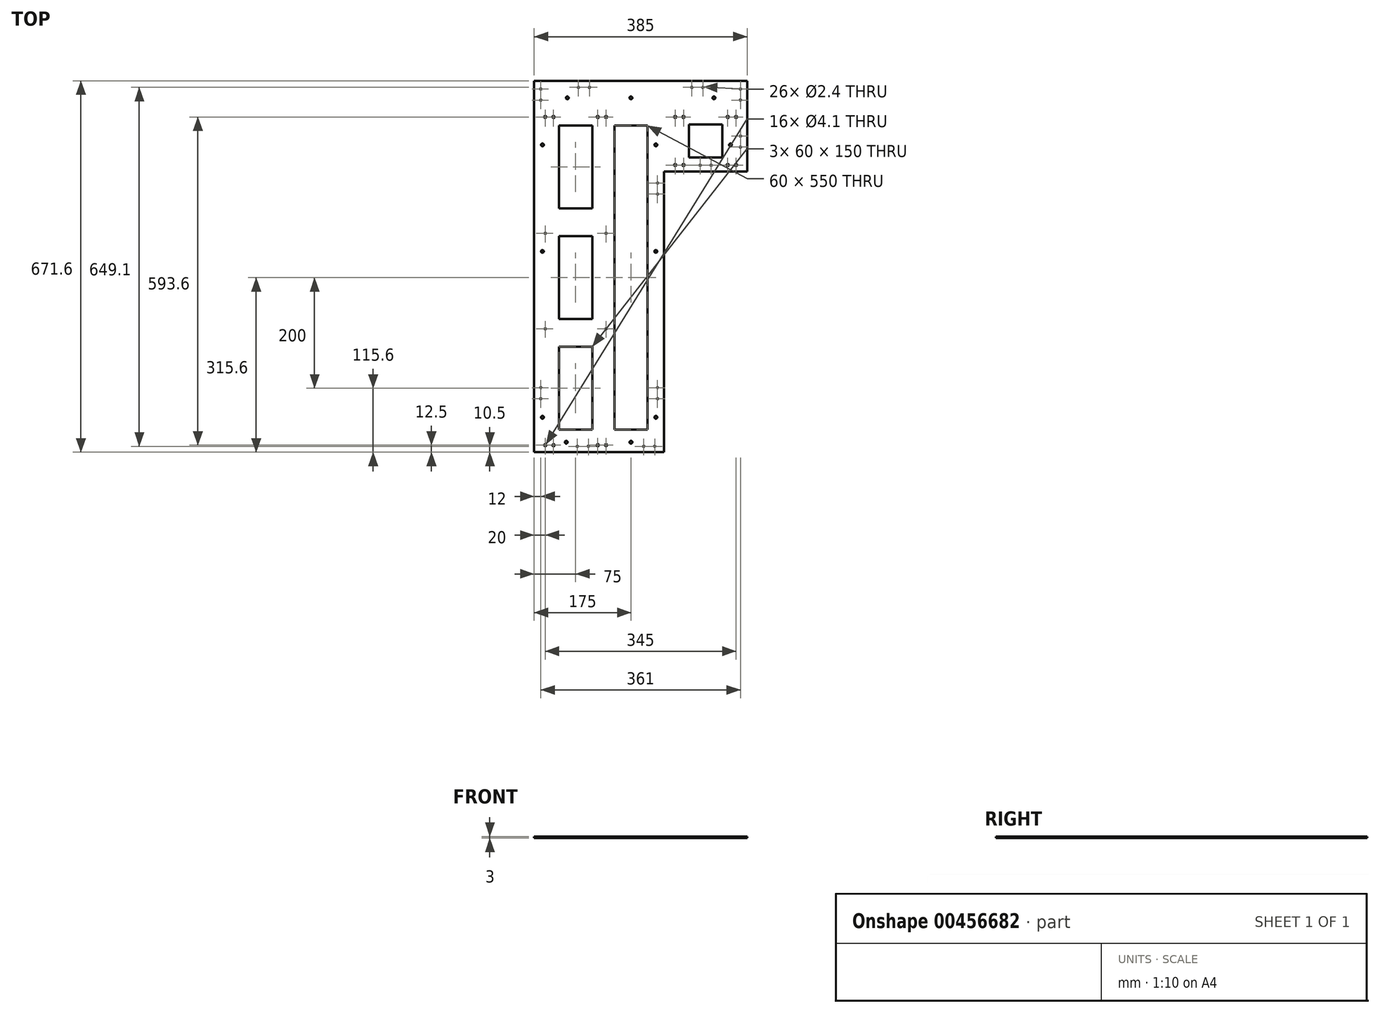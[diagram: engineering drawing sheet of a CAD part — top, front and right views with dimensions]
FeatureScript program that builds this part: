
annotation { "Feature Type Name" : "Feature", "Feature Type Description" : "" }
export const myFeature = defineFeature(function(context is Context, id is Id, definition is map)
    precondition{}
    {
        {
            var Q0;
            Q0=qCreatedBy(makeId("Top.planeOp"),FACE);
            var sketch = newSketch(context, id + "F0", { "sketchPlane" : qUnion([Q0])});
            skLineSegment(sketch, "E0.bottom", {"start": v(192.5, -53) * mm, "end": v(-192.5, -53) * mm});
            skLineSegment(sketch, "E0.top", {"start": v(192.5, 53) * mm, "end": v(-192.5, 53) * mm});
            skLineSegment(sketch, "E0.left", {"start": v(192.5, -53) * mm, "end": v(192.5, 53) * mm});
            skLineSegment(sketch, "E0.right", {"start": v(-192.5, -53) * mm, "end": v(-192.5, 53) * mm});
            skPoint(sketch, "E0.middle", {"position": v(0, 0) * mm});
            skCircle(sketch, "E1", {"center": v(-172.5, 43.5) * mm, "radius": 2.05 * mm});
            skCircle(sketch, "E2", {"center": v(-157.5, 43.5) * mm, "radius": 2.05 * mm});
            skLineSegment(sketch, "E3", {"start": v(-42.5, 73.43) * mm, "end": v(-42.5, -580.65) * mm, "construction": true});
            skLineSegment(sketch, "E4", {"start": v(42.5, 94.16) * mm, "end": v(42.5, -111.22) * mm, "construction": true});
            skCircle(sketch, "E5", {"center": v(-77.5, 43.5) * mm, "radius": 2.05 * mm});
            skCircle(sketch, "E6", {"center": v(-62.5, 43.5) * mm, "radius": 2.05 * mm});
            skCircle(sketch, "E7", {"center": v(62.5, 43.5) * mm, "radius": 2.05 * mm});
            skCircle(sketch, "E8", {"center": v(77.5, 43.5) * mm, "radius": 2.05 * mm});
            skCircle(sketch, "E9", {"center": v(157.5, 43.5) * mm, "radius": 2.05 * mm});
            skCircle(sketch, "E10", {"center": v(172.5, 43.5) * mm, "radius": 2.05 * mm});
            skLineSegment(sketch, "E11", {"start": v(202.9, -33.92) * mm, "end": v(25.15, -33.92) * mm, "construction": true});
            skCircle(sketch, "E12", {"center": v(172.5, -43.42) * mm, "radius": 2.05 * mm});
            skCircle(sketch, "E13", {"center": v(157.5, -43.42) * mm, "radius": 2.05 * mm});
            skCircle(sketch, "E14", {"center": v(62.5, -43.42) * mm, "radius": 2.05 * mm});
            skCircle(sketch, "E15", {"center": v(77.5, -43.42) * mm, "radius": 2.05 * mm});
            skLineSegment(sketch, "E16.bottom", {"start": v(-192.5, -53) * mm, "end": v(42.5, -53) * mm});
            skLineSegment(sketch, "E16.top", {"start": v(-192.5, -559.6) * mm, "end": v(42.5, -559.6) * mm});
            skLineSegment(sketch, "E16.left", {"start": v(-192.5, -53) * mm, "end": v(-192.5, -559.6) * mm});
            skLineSegment(sketch, "E16.right", {"start": v(42.5, -53) * mm, "end": v(42.5, -559.6) * mm});
            skLineSegment(sketch, "E17", {"start": v(-218.51, -539.6) * mm, "end": v(119.99, -539.6) * mm, "construction": true});
            skCircle(sketch, "E18", {"center": v(-172.5, -550.1) * mm, "radius": 2.05 * mm});
            skCircle(sketch, "E19", {"center": v(-157.5, -550.1) * mm, "radius": 2.05 * mm});
            skCircle(sketch, "E20", {"center": v(-77.5, -550.1) * mm, "radius": 2.05 * mm});
            skCircle(sketch, "E21", {"center": v(-62.5, -550.1) * mm, "radius": 2.05 * mm});
            skLineSegment(sketch, "E22", {"start": v(-117.5, 57.85) * mm, "end": v(-117.5, 33.54) * mm, "construction": true});
            skLineSegment(sketch, "E23", {"start": v(-153.12, 33) * mm, "end": v(-174.42, 33) * mm, "construction": true});
            skCircle(sketch, "E24", {"center": v(-172.5, -167) * mm, "radius": 1.2 * mm});
            skLineSegment(sketch, "E25", {"start": v(-176.5, -137.08) * mm, "end": v(-176.5, -144.67) * mm, "construction": true});
            skCircle(sketch, "E26", {"center": v(-172.5, -339.6) * mm, "radius": 1.2 * mm});
            skCircle(sketch, "E27", {"center": v(-62.5, -167) * mm, "radius": 1.2 * mm});
            skCircle(sketch, "E28", {"center": v(-62.5, -339.6) * mm, "radius": 1.2 * mm});
            skCircle(sketch, "E29", {"center": v(-177.5, -199.6) * mm, "radius": 2.5 * mm});
            skCircle(sketch, "E30", {"center": v(-134.5, -544.6) * mm, "radius": 2.5 * mm});
            skLineSegment(sketch, "E31.top", {"start": v(-192.5, -562.6) * mm, "end": v(42.5, -562.6) * mm});
            skLineSegment(sketch, "E31.left", {"start": v(-192.5, -559.6) * mm, "end": v(-192.5, -562.6) * mm});
            skLineSegment(sketch, "E31.right", {"start": v(42.5, -559.6) * mm, "end": v(42.5, -562.6) * mm});
            skCircle(sketch, "E32", {"center": v(-177.5, -499.6) * mm, "radius": 2.5 * mm});
            skCircle(sketch, "E33", {"center": v(-177.5, -7) * mm, "radius": 2.5 * mm});
            skCircle(sketch, "E34", {"center": v(27.5, -199.6) * mm, "radius": 2.5 * mm});
            skCircle(sketch, "E35", {"center": v(-17.5, -544.6) * mm, "radius": 2.5 * mm});
            skCircle(sketch, "E36", {"center": v(27.5, -499.6) * mm, "radius": 2.5 * mm});
            skCircle(sketch, "E37", {"center": v(27.5, -7) * mm, "radius": 2.5 * mm});
            skCircle(sketch, "E38", {"center": v(-132.5, 78) * mm, "radius": 2.5 * mm});
            skCircle(sketch, "E39", {"center": v(132.5, 78) * mm, "radius": 2.5 * mm});
            skCircle(sketch, "E40", {"center": v(-17.5, 78) * mm, "radius": 2.5 * mm});
            skLineSegment(sketch, "E41.bottom", {"start": v(42.5, -53) * mm, "end": v(192.5, -53) * mm});
            skLineSegment(sketch, "E41.top", {"start": v(42.5, -55) * mm, "end": v(192.5, -55) * mm});
            skLineSegment(sketch, "E41.left", {"start": v(42.5, -53) * mm, "end": v(42.5, -55) * mm});
            skLineSegment(sketch, "E41.right", {"start": v(192.5, -53) * mm, "end": v(192.5, -55) * mm});
            skLineSegment(sketch, "E42", {"start": v(-192.5, 53) * mm, "end": v(-192.5, 109) * mm});
            skLineSegment(sketch, "E43", {"start": v(-192.5, 109) * mm, "end": v(192.5, 109) * mm});
            skLineSegment(sketch, "E44", {"start": v(192.5, 109) * mm, "end": v(192.5, 53) * mm});
            skCircle(sketch, "E45", {"center": v(162.5, -7) * mm, "radius": 2.5 * mm});
            skSolve(sketch);
        }
        {
            var Q0;
            Q0=qSketchRegion(id+"F0",true);
            extrude(context, id + "F1", {"entities" : qUnion([Q0]), "depth" : 3 * mm});
        }
        {
            var Q0;
            Q0=makeQuery(id+"F1.opExtrude","CAP_FACE",FACE,{"disambiguationData":[OSD([sQuery(id+"F0.wireOp",EDGE,"E0.bottom"),sQuery(id+"F0.wireOp",EDGE,"E0.top"),sQuery(id+"F0.wireOp",EDGE,"E0.left"),sQuery(id+"F0.wireOp",EDGE,"E0.right"),sQuery(id+"F0.wireOp",EDGE,"E1"),sQuery(id+"F0.wireOp",EDGE,"E2"),sQuery(id+"F0.wireOp",EDGE,"E5"),sQuery(id+"F0.wireOp",EDGE,"E6"),sQuery(id+"F0.wireOp",EDGE,"E7"),sQuery(id+"F0.wireOp",EDGE,"E8"),sQuery(id+"F0.wireOp",EDGE,"E9"),sQuery(id+"F0.wireOp",EDGE,"E10"),sQuery(id+"F0.wireOp",EDGE,"E12"),sQuery(id+"F0.wireOp",EDGE,"E13"),sQuery(id+"F0.wireOp",EDGE,"E14"),sQuery(id+"F0.wireOp",EDGE,"E15"),sQuery(id+"F0.wireOp",EDGE,"E16.top"),sQuery(id+"F0.wireOp",EDGE,"E16.left"),sQuery(id+"F0.wireOp",EDGE,"E16.right"),sQuery(id+"F0.wireOp",EDGE,"E18"),sQuery(id+"F0.wireOp",EDGE,"E19"),sQuery(id+"F0.wireOp",EDGE,"E20"),sQuery(id+"F0.wireOp",EDGE,"E21")])],"isStart":false});
            var sketch = newSketch(context, id + "F2", { "sketchPlane" : qUnion([Q0])});
            skLineSegment(sketch, "E46.bottom", {"start": v(-87.5, -122) * mm, "end": v(-147.5, -122) * mm});
            skLineSegment(sketch, "E46.top", {"start": v(-87.5, 28) * mm, "end": v(-147.5, 28) * mm});
            skLineSegment(sketch, "E46.left", {"start": v(-87.5, -122) * mm, "end": v(-87.5, 28) * mm});
            skLineSegment(sketch, "E46.right", {"start": v(-147.5, -122) * mm, "end": v(-147.5, 28) * mm});
            skPoint(sketch, "E46.middle", {"position": v(-117.5, -47) * mm});
            skLineSegment(sketch, "E47.bottom", {"start": v(-87.5, -172) * mm, "end": v(-147.5, -172) * mm});
            skLineSegment(sketch, "E47.top", {"start": v(-87.5, -322) * mm, "end": v(-147.5, -322) * mm});
            skLineSegment(sketch, "E47.left", {"start": v(-87.5, -172) * mm, "end": v(-87.5, -322) * mm});
            skLineSegment(sketch, "E47.right", {"start": v(-147.5, -172) * mm, "end": v(-147.5, -322) * mm});
            skPoint(sketch, "E47.middle", {"position": v(-117.5, -247) * mm});
            skLineSegment(sketch, "E48", {"start": v(-117.5, 70.25) * mm, "end": v(-117.5, -57.76) * mm, "construction": true});
            skLineSegment(sketch, "E49", {"start": v(117.5, 72.9) * mm, "end": v(117.5, -109.15) * mm, "construction": true});
            skLineSegment(sketch, "E50.bottom", {"start": v(147.5, -30) * mm, "end": v(87.5, -30) * mm});
            skLineSegment(sketch, "E50.top", {"start": v(147.5, 30) * mm, "end": v(87.5, 30) * mm});
            skLineSegment(sketch, "E50.left", {"start": v(147.5, -30) * mm, "end": v(147.5, 30) * mm});
            skLineSegment(sketch, "E50.right", {"start": v(87.5, -30) * mm, "end": v(87.5, 30) * mm});
            skPoint(sketch, "E50.middle", {"position": v(117.5, 0) * mm});
            skLineSegment(sketch, "E51.bottom", {"start": v(-87.5, -372) * mm, "end": v(-147.5, -372) * mm});
            skLineSegment(sketch, "E51.top", {"start": v(-87.5, -522) * mm, "end": v(-147.5, -522) * mm});
            skLineSegment(sketch, "E51.left", {"start": v(-87.5, -372) * mm, "end": v(-87.5, -522) * mm});
            skLineSegment(sketch, "E51.right", {"start": v(-147.5, -372) * mm, "end": v(-147.5, -522) * mm});
            skPoint(sketch, "E51.middle", {"position": v(-117.5, -447) * mm});
            skLineSegment(sketch, "E52", {"start": v(-42.5, 117.64) * mm, "end": v(-42.5, -137.41) * mm, "construction": true});
            skLineSegment(sketch, "E53.bottom", {"start": v(-47.5, 28) * mm, "end": v(12.5, 28) * mm});
            skLineSegment(sketch, "E53.top", {"start": v(-47.5, -522) * mm, "end": v(12.5, -522) * mm});
            skLineSegment(sketch, "E53.left", {"start": v(-47.5, 28) * mm, "end": v(-47.5, -522) * mm});
            skLineSegment(sketch, "E53.right", {"start": v(12.5, 28) * mm, "end": v(12.5, -522) * mm});
            skSolve(sketch);
        }
        {
            var Q0;
            Q0=qSketchRegion(id+"F2",true);
            extrude(context, id + "F3", {"entities" : qUnion([Q0]), "operationType" : NewBodyOperationType.REMOVE, "oppositeDirection" : true, "depth" : 25 * mm});
        }
        {
            var Q0;
            Q0=makeQuery(id+"F2O8r8H572E9jEw_1.boolean.opBoolean","MERGE",FACE,{"derivedFrom":[makeQuery(id+"F1.opExtrude","CAP_FACE",FACE,{"disambiguationData":[OSD([sQuery(id+"F0.wireOp",EDGE,"E0.top"),sQuery(id+"F0.wireOp",EDGE,"E0.left"),sQuery(id+"F0.wireOp",EDGE,"E0.right"),sQuery(id+"F0.wireOp",EDGE,"E1"),sQuery(id+"F0.wireOp",EDGE,"E2"),sQuery(id+"F0.wireOp",EDGE,"E5"),sQuery(id+"F0.wireOp",EDGE,"E6"),sQuery(id+"F0.wireOp",EDGE,"E7"),sQuery(id+"F0.wireOp",EDGE,"E8"),sQuery(id+"F0.wireOp",EDGE,"E9"),sQuery(id+"F0.wireOp",EDGE,"E10"),sQuery(id+"F0.wireOp",EDGE,"E12"),sQuery(id+"F0.wireOp",EDGE,"E13"),sQuery(id+"F0.wireOp",EDGE,"E14"),sQuery(id+"F0.wireOp",EDGE,"E15"),sQuery(id+"F0.wireOp",EDGE,"E16.left"),sQuery(id+"F0.wireOp",EDGE,"E16.right"),sQuery(id+"F0.wireOp",EDGE,"E18"),sQuery(id+"F0.wireOp",EDGE,"E19"),sQuery(id+"F0.wireOp",EDGE,"E20"),sQuery(id+"F0.wireOp",EDGE,"E21"),sQuery(id+"F0.wireOp",EDGE,"E24"),sQuery(id+"F0.wireOp",EDGE,"E26"),sQuery(id+"F0.wireOp",EDGE,"E27"),sQuery(id+"F0.wireOp",EDGE,"E28"),sQuery(id+"F0.wireOp",EDGE,"E29"),sQuery(id+"F0.wireOp",EDGE,"E30"),sQuery(id+"F0.wireOp",EDGE,"E31.top"),sQuery(id+"F0.wireOp",EDGE,"E31.left"),sQuery(id+"F0.wireOp",EDGE,"E31.right"),sQuery(id+"F0.wireOp",EDGE,"E32"),sQuery(id+"F0.wireOp",EDGE,"E33"),sQuery(id+"F0.wireOp",EDGE,"E34"),sQuery(id+"F0.wireOp",EDGE,"E35"),sQuery(id+"F0.wireOp",EDGE,"E36"),sQuery(id+"F0.wireOp",EDGE,"E37"),sQuery(id+"F0.wireOp",EDGE,"E38"),sQuery(id+"F0.wireOp",EDGE,"E39"),sQuery(id+"F0.wireOp",EDGE,"TjULq03c-Gpqh-KJec-qWmQ-0YuIlEzygd5B"),sQuery(id+"F0.wireOp",EDGE,"lCEzzgQS-Qvkz-X3D3-LDLk-qSDPH7AwNQJv"),sQuery(id+"F0.wireOp",EDGE,"E40"),sQuery(id+"F0.wireOp",EDGE,"E41.top"),sQuery(id+"F0.wireOp",EDGE,"E41.right")])],"isStart":false}),makeQuery(id+"F2O8r8H572E9jEw_1.opExtrude","CAP_FACE",FACE,{"disambiguationData":[OSD([sQuery(id+"FIaY4WBdf4dioWf_1.wireOp",EDGE,"mXuLmiP2-nhxb-6Rn9-Rc8G-rbgXLuEv7Aki.bottom"),sQuery(id+"FIaY4WBdf4dioWf_1.wireOp",EDGE,"mXuLmiP2-nhxb-6Rn9-Rc8G-rbgXLuEv7Aki.top"),sQuery(id+"FIaY4WBdf4dioWf_1.wireOp",EDGE,"mXuLmiP2-nhxb-6Rn9-Rc8G-rbgXLuEv7Aki.left"),sQuery(id+"FIaY4WBdf4dioWf_1.wireOp",EDGE,"mXuLmiP2-nhxb-6Rn9-Rc8G-rbgXLuEv7Aki.right")])],"isStart":false})]});
            var sketch = newSketch(context, id + "F4", { "sketchPlane" : qUnion([Q0])});
            skCircle(sketch, "E54", {"center": v(-180.5, 94) * mm, "radius": 1.2 * mm});
            skCircle(sketch, "E55", {"center": v(-180.5, 74) * mm, "radius": 1.2 * mm});
            skCircle(sketch, "E56", {"center": v(-180.5, -446) * mm, "radius": 1.2 * mm});
            skCircle(sketch, "E57", {"center": v(-180.5, -466) * mm, "radius": 1.2 * mm});
            skCircle(sketch, "E58", {"center": v(30.5, -446) * mm, "radius": 1.2 * mm});
            skCircle(sketch, "E59", {"center": v(30.5, -466) * mm, "radius": 1.2 * mm});
            skCircle(sketch, "E60", {"center": v(30.5, -76) * mm, "radius": 1.2 * mm});
            skCircle(sketch, "E61", {"center": v(30.5, -96) * mm, "radius": 1.2 * mm});
            skCircle(sketch, "E62", {"center": v(180.5, 94) * mm, "radius": 1.2 * mm});
            skCircle(sketch, "E63", {"center": v(180.5, 74) * mm, "radius": 1.2 * mm});
            skCircle(sketch, "E64", {"center": v(180.5, 9) * mm, "radius": 1.2 * mm});
            skCircle(sketch, "E65", {"center": v(180.5, -11) * mm, "radius": 1.2 * mm});
            skCircle(sketch, "E66", {"center": v(-114.5, -552.1) * mm, "radius": 1.2 * mm});
            skCircle(sketch, "E67", {"center": v(-94.5, -552.1) * mm, "radius": 1.2 * mm});
            skCircle(sketch, "E68", {"center": v(5.5, -552.1) * mm, "radius": 1.2 * mm});
            skCircle(sketch, "E69", {"center": v(25.5, -552.1) * mm, "radius": 1.2 * mm});
            skCircle(sketch, "E70", {"center": v(-112.5, 97) * mm, "radius": 1.2 * mm});
            skCircle(sketch, "E71", {"center": v(-92.5, 97) * mm, "radius": 1.2 * mm});
            skCircle(sketch, "E72", {"center": v(92.5, 97) * mm, "radius": 1.2 * mm});
            skCircle(sketch, "E73", {"center": v(112.5, 97) * mm, "radius": 1.2 * mm});
            skCircle(sketch, "E74", {"center": v(107.5, -43.8) * mm, "radius": 1.2 * mm});
            skCircle(sketch, "E75", {"center": v(127.5, -43.8) * mm, "radius": 1.2 * mm});
            skSolve(sketch);
        }
        {
            var Q0;
            Q0=qSketchRegion(id+"F4",true);
            extrude(context, id + "F5", {"entities" : qUnion([Q0]), "operationType" : NewBodyOperationType.REMOVE, "oppositeDirection" : true, "depth" : 25 * mm});
        }
    });
